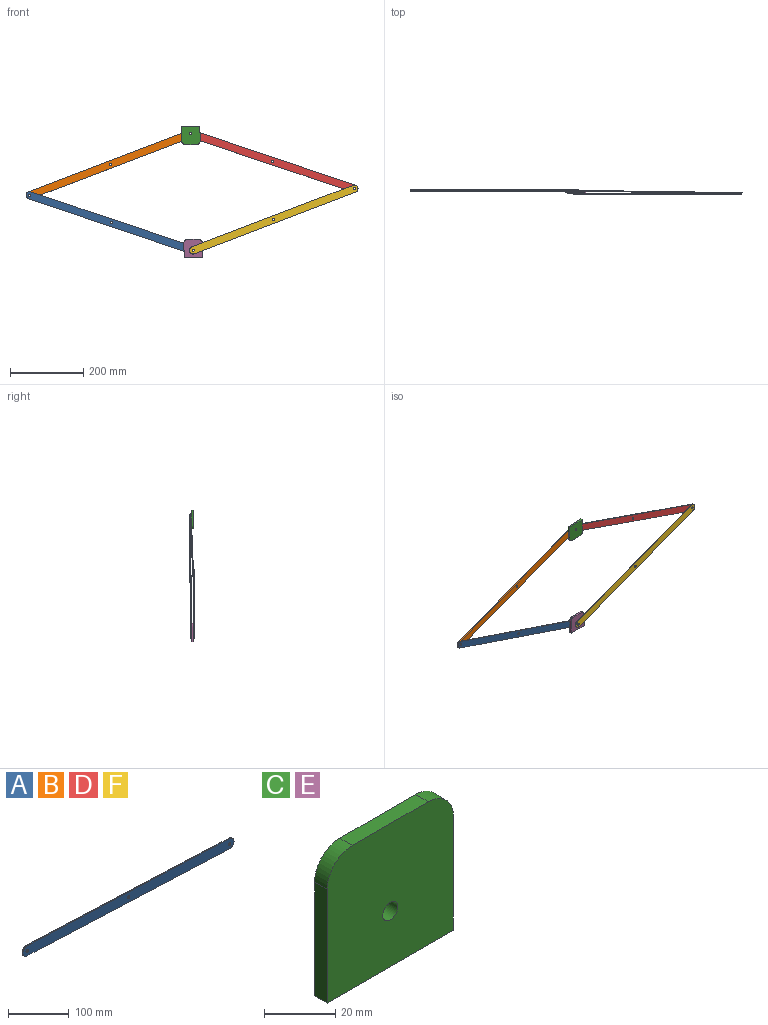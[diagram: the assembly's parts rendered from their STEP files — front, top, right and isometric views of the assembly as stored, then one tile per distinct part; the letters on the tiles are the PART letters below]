
ASSEMBLY  parts=6 mates=7
PART A: 9 faces, bbox 490x2x40 mm
  f0: plane 470x20mm, normal (-0.04,0,-1), area 940.9mm2, adj f1,f5,f7,f8
  f1: cylinder r=10mm len=19.99mm, axis (0,-1,0), area 62.8mm2, adj f0,f2,f7,f8
  f2: plane 470x20mm, normal (0.04,0,1), area 940.9mm2, adj f1,f5,f7,f8
  f3: cylinder r=3mm len=6mm, axis (0,-1,0), area 37.7mm2, adj f7,f8
  f4: cylinder r=3mm len=6mm, axis (0,-1,0), area 37.7mm2, adj f7,f8
  f5: cylinder r=10mm len=19.99mm, axis (0,-1,0), area 62.8mm2, adj f0,f2,f7,f8
  f6: cylinder r=3mm len=6mm, axis (0,-1,0), area 37.7mm2, adj f7,f8
  f7: plane 490x40mm, normal (0,1,0), area 9637.8mm2, adj f0,f1,f2,f3,f4,f5,f6
  f8: plane 490x40mm, normal (0,-1,0), area 9637.8mm2, adj f0,f1,f2,f3,f4,f5,f6
PART B: same geometry as A
PART C: 9 faces, bbox 50x5x49 mm
  f0: plane 39x5mm, normal (-1,0,0), area 195mm2, adj f1,f5,f7,f8
  f1: plane 49.99x5mm, normal (0,0,-1), area 249.9mm2, adj f0,f2,f7,f8
  f2: plane 39x5mm, normal (1,0,0), area 195mm2, adj f1,f3,f7,f8
  f3: cylinder r=10mm len=10mm, axis (0,1,0), area 78.5mm2, adj f2,f4,f7,f8
  f4: plane 29.99x5mm, normal (0,0,1), area 149.9mm2, adj f3,f5,f7,f8
  f5: cylinder r=10mm len=10mm, axis (0,1,0), area 78.5mm2, adj f0,f4,f7,f8
  f6: cylinder r=3mm len=6mm, axis (0,1,0), area 94.2mm2, adj f7,f8
  f7: plane 49.99x49mm, normal (0,-1,0), area 2378.3mm2, adj f0,f1,f2,f3,f4,f5,f6
  f8: plane 49.99x49mm, normal (0,1,0), area 2378.3mm2, adj f0,f1,f2,f3,f4,f5,f6
PART D: same geometry as A
PART E: same geometry as C
PART F: same geometry as A
PLACE A rot(axis=(0,1,0),16.2deg) t=(1298.51,-50.41,-680.15)mm
PLACE B rot(axis=(0,1,-0.01),156.6deg) t=(-1795.56,-57.81,-1273.16)mm
PLACE C rot(axis=(0,1,0),178.9deg) t=(-1233.54,-51.33,-558.82)mm
PLACE D rot(axis=(-0.07,1,-0.03),16.2deg) t=(1740.09,-68.52,-517.81)mm
PLACE E rot(axis=(-0.06,-1,0.02),1.2deg) t=(908.58,-50.05,-267.99)mm
PLACE F rot(axis=(0,1,0),156.6deg) t=(-1351.8,-60.46,-1417.87)mm
MATE revolute A.f1 <-> E.f6  axis (0,-1,0) through (-159.15,-363.73,-572.13)mm
MATE revolute F.f1 <-> E.f6  axis (0,-1,0) through (-159.15,-368.73,-572.12)mm
MATE ball B.f1 <-> A.f4  axis (-0.01,-1,0.02) through (-604.94,-361.73,-421.89)mm
MATE ball C.f6 <-> D.f4  axis (0,1,0) through (-165.54,-363.34,-253.9)mm
MATE revolute D.f4 <-> B.f4  axis (0.01,1,-0.02) through (-165.52,-361.34,-253.94)mm
MATE ball D.f1 <-> F.f4  axis (-0.01,-1,0.02) through (280.24,-369.34,-404.07)mm
MATE slider C.f1 <-> E.f1  axis (-0.02,0,1) through (-165.92,-365.81,-234.9)mm
